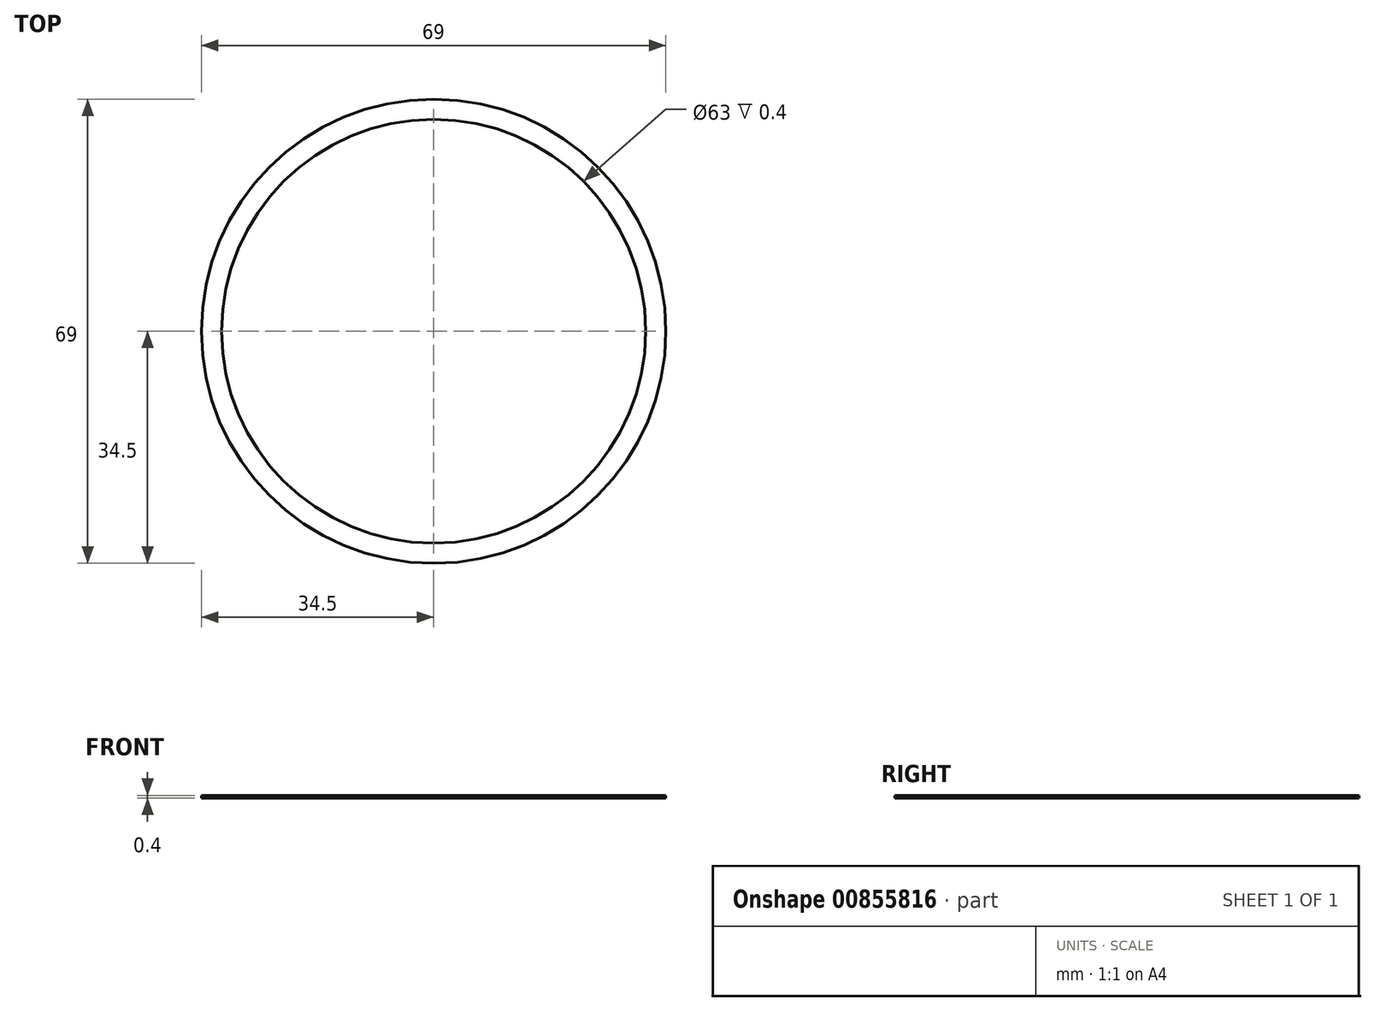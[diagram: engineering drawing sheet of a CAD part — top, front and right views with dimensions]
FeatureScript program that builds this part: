
annotation { "Feature Type Name" : "Feature", "Feature Type Description" : "" }
export const myFeature = defineFeature(function(context is Context, id is Id, definition is map)
    precondition{}
    {
        {
            var Q0;
            Q0=qCreatedBy(makeId("Top.planeOp"),FACE);
            var sketch = newSketch(context, id + "F0", { "sketchPlane" : qUnion([Q0])});
            skCircle(sketch, "E0", {"center": v(0, 0) * mm, "radius": 31.5 * mm});
            skCircle(sketch, "E1", {"center": v(0, 0) * mm, "radius": 34.5 * mm});
            skSolve(sketch);
        }
        {
            var Q0;
            Q0 = qSketchRegion(id + "F0", true);
            extrude(context, id + "F1", {"entities" : qUnion([Q0]), "depth" : .4 * mm, "offsetDistance" : 25 * mm});
        }
    });
